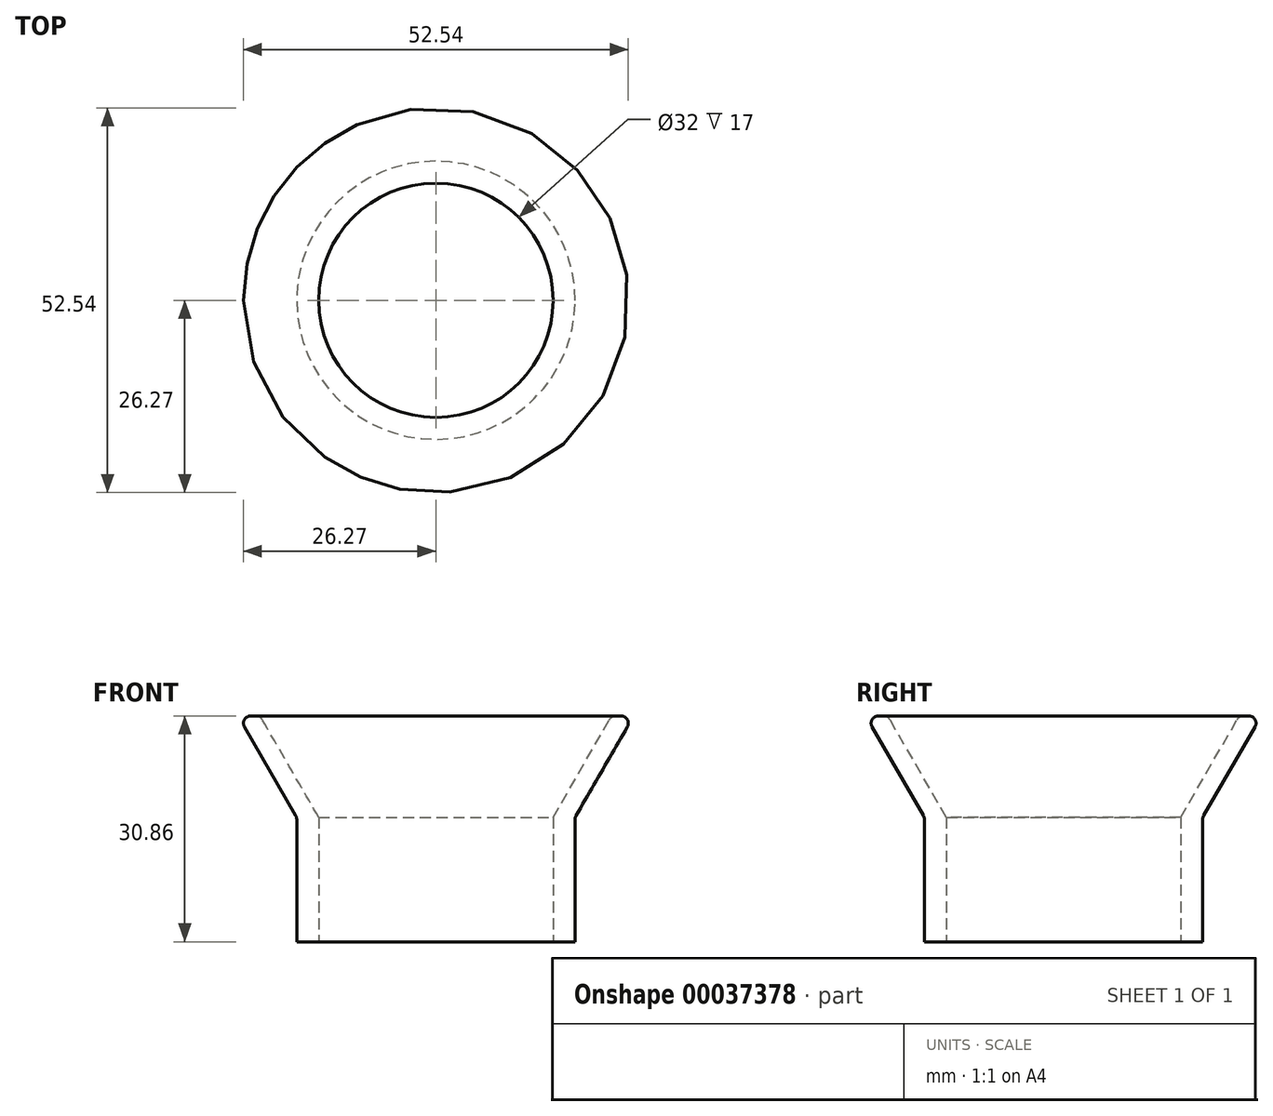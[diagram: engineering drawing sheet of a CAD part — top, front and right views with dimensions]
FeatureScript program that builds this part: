
annotation { "Feature Type Name" : "Feature", "Feature Type Description" : "" }
export const myFeature = defineFeature(function(context is Context, id is Id, definition is map)
    precondition{}
    {
        {
            var Q0;
            Q0=qCreatedBy(makeId("Front.planeOp"),FACE);
            var sketch = newSketch(context, id + "F0", { "sketchPlane" : qUnion([Q0])});
            skLineSegment(sketch, "E0", {"start": v(-16, 0) * mm, "end": v(-19, 0) * mm});
            skLineSegment(sketch, "E1", {"start": v(-19, 0) * mm, "end": v(-19, 17) * mm});
            skLineSegment(sketch, "E2", {"start": v(-16, 0) * mm, "end": v(-16, 17) * mm});
            skLineSegment(sketch, "E3", {"start": v(-19, 17) * mm, "end": v(-27, 30.86) * mm});
            skLineSegment(sketch, "E4", {"start": v(-16, 17) * mm, "end": v(-24, 30.86) * mm});
            skLineSegment(sketch, "E5", {"start": v(-24, 30.86) * mm, "end": v(-27, 30.86) * mm});
            skLineSegment(sketch, "E6", {"start": v(0, -8.41) * mm, "end": v(0, 22.66) * mm});
            skSolve(sketch);
        }
        {
            var Q0;
            Q0=makeQuery(id+"F0.imprint","IMPRINT",FACE,{"disambiguationData":[TD([[makeQuery(id+"F0.imprint","IMPRINT",EDGE,{"derivedFrom":sQuery(id+"F0.wireOp",EDGE,"E0")}),-1.0]])]});
            var Q1;
            Q1=sQuery(id+"F0.wireOp",EDGE,"E6");
            revolve(context, id + "F1", {"entities" : qUnion([Q0]), "axis" : qUnion([Q1]), "revolveType" : RevolveType.FULL});
        }
        {
            var Q0;
            Q0=makeQuery(id+"F1.opRevolve","SWEPT_FACE",FACE,{"disambiguationData":[OSD([sQuery(id+"F0.wireOp",EDGE,"E5")])]});
            var Q1;
            Q1=makeQuery(id+"F1.opRevolve","SWEPT_EDGE",EDGE,{"disambiguationData":[OSD([sQuery(id+"F0.wireOp",EDGE,"E1"),sQuery(id+"F0.wireOp",EDGE,"E3")])]});
            fillet(context, id + "F2", {"entities" : qUnion([Q0, Q1]), "radius" : 1 * mm, "tangentPropagation" : true, "allowEdgeOverflow" : false});
        }
    });
